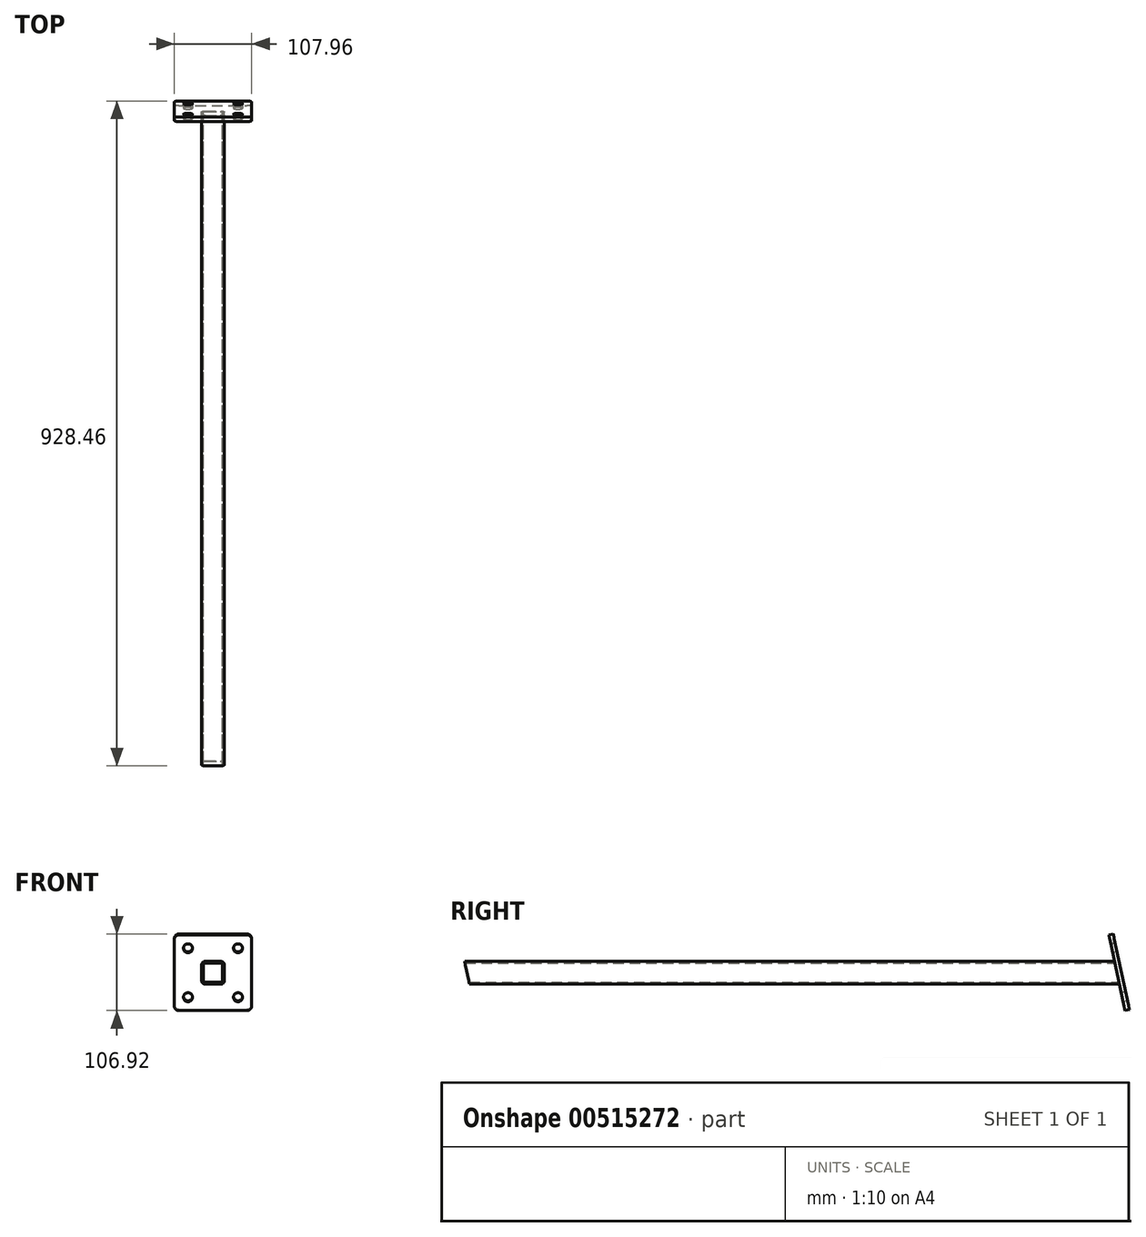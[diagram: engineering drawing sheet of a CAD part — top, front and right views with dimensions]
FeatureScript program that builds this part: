
annotation { "Feature Type Name" : "Feature", "Feature Type Description" : "" }
export const myFeature = defineFeature(function(context is Context, id is Id, definition is map)
    precondition{}
    {
        {
            var Q0;
            Q0=qCreatedBy(makeId("Front.planeOp"),FACE);
            var sketch = newSketch(context, id + "F0", { "sketchPlane" : qUnion([Q0])});
            skLineSegment(sketch, "E0.bottom", {"start": v(-15.87, 15.88) * mm, "end": v(15.88, 15.88) * mm});
            skLineSegment(sketch, "E0.top", {"start": v(-15.88, -15.88) * mm, "end": v(15.87, -15.88) * mm});
            skLineSegment(sketch, "E0.left", {"start": v(-15.87, 15.88) * mm, "end": v(-15.88, -15.88) * mm});
            skLineSegment(sketch, "E0.right", {"start": v(15.88, 15.88) * mm, "end": v(15.87, -15.88) * mm});
            skPoint(sketch, "E0.middle", {"position": v(0, 0) * mm});
            skLineSegment(sketch, "E1.0", {"start": v(13.46, 13.46) * mm, "end": v(13.46, -13.46) * mm});
            skLineSegment(sketch, "E1.1", {"start": v(-13.46, 13.46) * mm, "end": v(13.46, 13.46) * mm});
            skLineSegment(sketch, "E1.2", {"start": v(-13.46, 13.46) * mm, "end": v(-13.46, -13.46) * mm});
            skLineSegment(sketch, "E1.3", {"start": v(-13.46, -13.46) * mm, "end": v(13.46, -13.46) * mm});
            skSolve(sketch);
        }
        {
            var Q0;
            Q0=qSketchRegion(id+"F0",true);
            extrude(context, id + "F1", {"entities" : qUnion([Q0]), "endBound" : BoundingType.SYMMETRIC, "depth" : 914.4 * mm, "offsetDistance" : 25.4 * mm});
        }
        {
            var Q0;
            Q0=makeQuery(id+"F1.opExtrude","SWEPT_EDGE",EDGE,{"disambiguationData":[OSD([sQuery(id+"F0.wireOp",EDGE,"E0.top"),sQuery(id+"F0.wireOp",EDGE,"E0.right")])]});
            var Q1;
            Q1=makeQuery(id+"F1.opExtrude","SWEPT_EDGE",EDGE,{"disambiguationData":[OSD([sQuery(id+"F0.wireOp",EDGE,"E0.top"),sQuery(id+"F0.wireOp",EDGE,"E0.left")])]});
            var Q2;
            Q2=makeQuery(id+"F1.opExtrude","SWEPT_EDGE",EDGE,{"disambiguationData":[OSD([sQuery(id+"F0.wireOp",EDGE,"E0.bottom"),sQuery(id+"F0.wireOp",EDGE,"E0.left")])]});
            var Q3;
            Q3=makeQuery(id+"F1.opExtrude","SWEPT_EDGE",EDGE,{"disambiguationData":[OSD([sQuery(id+"F0.wireOp",EDGE,"E0.bottom"),sQuery(id+"F0.wireOp",EDGE,"E0.right")])]});
            fillet(context, id + "F2", {"entities" : qUnion([Q0, Q1, Q2, Q3]), "radius" : 4.78 * mm, "tangentPropagation" : true, "allowEdgeOverflow" : false});
        }
        {
            var Q0;
            Q0=makeQuery(id+"F1.opExtrude","SWEPT_EDGE",EDGE,{"disambiguationData":[OSD([sQuery(id+"F0.wireOp",EDGE,"E1.1"),sQuery(id+"F0.wireOp",EDGE,"E1.2")])]});
            var Q1;
            Q1=makeQuery(id+"F1.opExtrude","SWEPT_EDGE",EDGE,{"disambiguationData":[OSD([sQuery(id+"F0.wireOp",EDGE,"E1.0"),sQuery(id+"F0.wireOp",EDGE,"E1.1")])]});
            var Q2;
            Q2=makeQuery(id+"F1.opExtrude","SWEPT_EDGE",EDGE,{"disambiguationData":[OSD([sQuery(id+"F0.wireOp",EDGE,"E1.2"),sQuery(id+"F0.wireOp",EDGE,"E1.3")])]});
            var Q3;
            Q3=makeQuery(id+"F1.opExtrude","SWEPT_EDGE",EDGE,{"disambiguationData":[OSD([sQuery(id+"F0.wireOp",EDGE,"E1.0"),sQuery(id+"F0.wireOp",EDGE,"E1.3")])]});
            fillet(context, id + "F3", {"entities" : qUnion([Q0, Q1, Q2, Q3]), "radius" : 3.17 * mm, "tangentPropagation" : true, "allowEdgeOverflow" : false});
        }
        {
            var Q0;
            Q0=makeQuery(id+"F1.opExtrude","SWEPT_FACE",FACE,{"disambiguationData":[OSD([sQuery(id+"F0.wireOp",EDGE,"E0.right")])]});
            var sketch = newSketch(context, id + "F4", { "sketchPlane" : qUnion([Q0])});
            skLineSegment(sketch, "E2", {"start": v(-457.2, 15.88) * mm, "end": v(-457.2, -15.87) * mm});
            skLineSegment(sketch, "E3", {"start": v(-457.2, 15.88) * mm, "end": v(-450.45, -15.87) * mm});
            skLineSegment(sketch, "E4", {"start": v(-450.45, -15.87) * mm, "end": v(-457.2, -15.87) * mm});
            skLineSegment(sketch, "E5.MirrorCS", {"start": v(450.45, 15.88) * mm, "end": v(457.2, 15.88) * mm});
            skLineSegment(sketch, "E6.MirrorCS", {"start": v(450.45, 15.88) * mm, "end": v(457.2, -15.88) * mm});
            skLineSegment(sketch, "E7.MirrorCS", {"start": v(457.2, 15.88) * mm, "end": v(457.2, -15.88) * mm});
            skSolve(sketch);
        }
        {
            var Q0;
            Q0 = qSketchRegion(id + "F4", true);
            extrude(context, id + "F5", {"entities" : qUnion([Q0]), "operationType" : NewBodyOperationType.REMOVE, "endBound" : BoundingType.THROUGH_ALL, "oppositeDirection" : true, "depth" : 25.4 * mm, "offsetDistance" : 25.4 * mm});
        }
        {
            var Q0;
            Q0=makeQuery(id+"F5.boolean.opBoolean","COPY",FACE,{"derivedFrom":makeQuery(id+"F5.opExtrude","SWEPT_FACE",FACE,{"disambiguationData":[OSD([sQuery(id+"F4.wireOp",EDGE,"E6.MirrorCS")])]})});
            var sketch = newSketch(context, id + "F6", { "sketchPlane" : qUnion([Q0])});
            skLineSegment(sketch, "E8.bottom", {"start": v(47.63, -148.33) * mm, "end": v(-47.62, -148.33) * mm});
            skLineSegment(sketch, "E8.top", {"start": v(47.63, -40.38) * mm, "end": v(-47.62, -40.38) * mm});
            skLineSegment(sketch, "E8.left", {"start": v(53.98, -141.98) * mm, "end": v(53.98, -46.73) * mm});
            skLineSegment(sketch, "E8.right", {"start": v(-53.97, -141.98) * mm, "end": v(-53.97, -46.73) * mm});
            skPoint(sketch, "E8.middle", {"position": v(0, -94.36) * mm});
            skPoint(sketch, "E8.middle.positionSnap0", {"position": v(15.88, -94.36) * mm});
            skPoint(sketch, "E8.centerSnap0", {"position": v(15.88, -94.36) * mm});
            skPoint(sketch, "E9.visualSharp", {"position": v(-53.97, -40.38) * mm});
            skArc(sketch, "E9.filletArc", {"start": v(-47.62, -40.38) * mm, "mid": v(-52.12, -42.24) * mm, "end": v(-53.97, -46.73) * mm});
            skPoint(sketch, "E10.visualSharp", {"position": v(53.98, -40.38) * mm});
            skArc(sketch, "E10.filletArc", {"start": v(53.97, -46.73) * mm, "mid": v(52.12, -42.24) * mm, "end": v(47.63, -40.38) * mm});
            skPoint(sketch, "E11.visualSharp", {"position": v(53.98, -148.33) * mm});
            skArc(sketch, "E11.filletArc", {"start": v(47.63, -148.33) * mm, "mid": v(52.12, -146.47) * mm, "end": v(53.97, -141.98) * mm});
            skPoint(sketch, "E12.visualSharp", {"position": v(-53.97, -148.33) * mm});
            skArc(sketch, "E12.filletArc", {"start": v(-53.97, -141.98) * mm, "mid": v(-52.12, -146.47) * mm, "end": v(-47.62, -148.33) * mm});
            skCircle(sketch, "E13", {"center": v(-34.92, -59.43) * mm, "radius": 6.35 * mm});
            skCircle(sketch, "E14.MirrorC", {"center": v(34.93, -59.43) * mm, "radius": 6.35 * mm});
            skCircle(sketch, "E15.MirrorC", {"center": v(-34.92, -129.28) * mm, "radius": 6.35 * mm});
            skCircle(sketch, "E16.MirrorC", {"center": v(34.93, -129.28) * mm, "radius": 6.35 * mm});
            skSolve(sketch);
        }
        {
            var Q0;
            Q0 = qSketchRegion(id + "F6", true);
            extrude(context, id + "F7", {"entities" : qUnion([Q0]), "operationType" : NewBodyOperationType.ADD, "depth" : 6.35 * mm, "offsetDistance" : 25.4 * mm});
        }
    });
